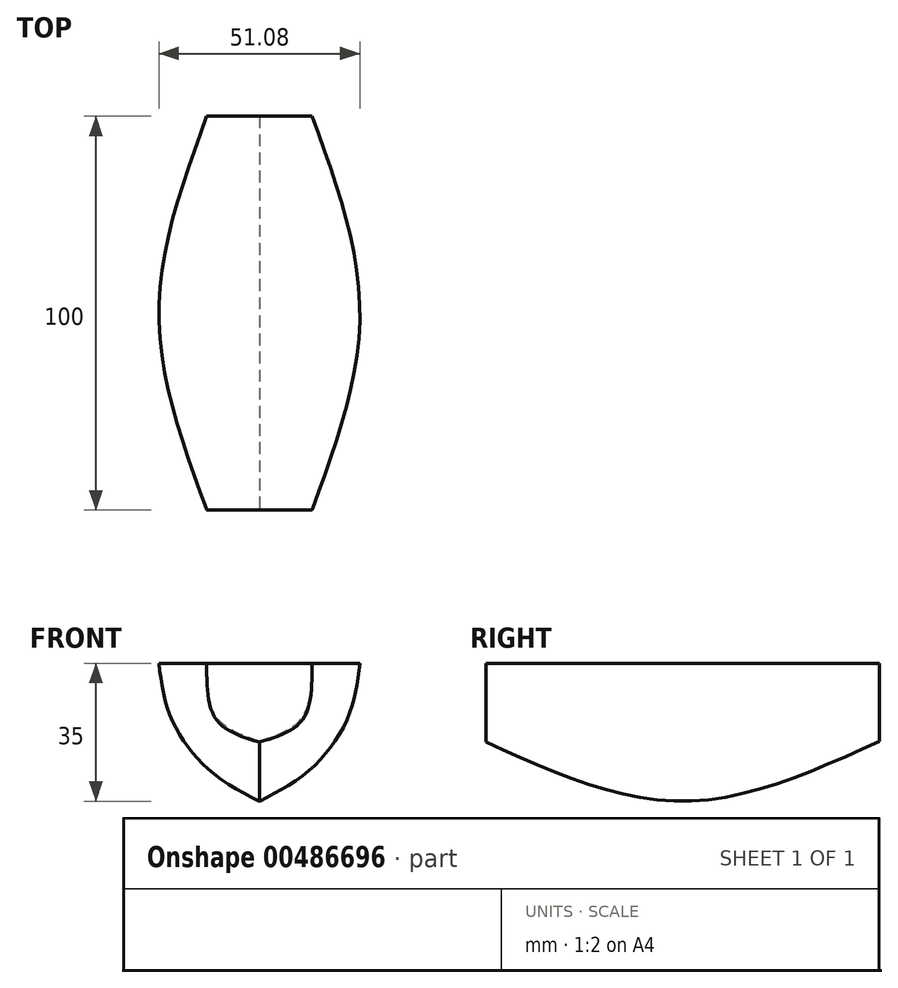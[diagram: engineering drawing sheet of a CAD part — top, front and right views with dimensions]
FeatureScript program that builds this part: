
annotation { "Feature Type Name" : "Feature", "Feature Type Description" : "" }
export const myFeature = defineFeature(function(context is Context, id is Id, definition is map)
    precondition{}
    {
        {
            var Q0;
            Q0=qCreatedBy(makeId("Front.planeOp"),FACE);
            cPlane(context, id + "F0", {"entities" : qUnion([Q0]), "cplaneType" : CPlaneType.OFFSET, "offset" : 50 * mm, "width" : 150 * mm, "height" : 150 * mm});
        }
        {
            var Q0;
            Q0=qCreatedBy(makeId("Front.planeOp"),FACE);
            cPlane(context, id + "F1", {"entities" : qUnion([Q0]), "cplaneType" : CPlaneType.OFFSET, "offset" : 50 * mm, "oppositeDirection" : true, "width" : 150 * mm, "height" : 150 * mm});
        }
        {
            var Q0;
            Q0=qCreatedBy(id+"F0.planeOp",FACE);
            var sketch = newSketch(context, id + "F2", { "sketchPlane" : qUnion([Q0])});
            skLineSegment(sketch, "E0", {"start": v(0, 0) * mm, "end": v(0, -20) * mm});
            skFitSpline(sketch, "E1", {"points": [v(0, -20) * mm, v(-10.95, -14.3) * mm, v(-13.38, 0) * mm], "startDerivative": vector(-27.16, 8.16) * mm, "endDerivative": vector(0.04, 31.53) * mm});
            skLineSegment(sketch, "E2", {"start": v(-13.38, 0) * mm, "end": v(0, 0) * mm});
            skSolve(sketch);
        }
        {
            var Q0;
            Q0=qCreatedBy(makeId("Front.planeOp"),FACE);
            var sketch = newSketch(context, id + "F3", { "sketchPlane" : qUnion([Q0])});
            skLineSegment(sketch, "E3", {"start": v(0, 0) * mm, "end": v(0, -35) * mm});
            skFitSpline(sketch, "E4", {"points": [v(0, -35) * mm, v(-12.77, -27.06) * mm, v(-22.5, -13.68) * mm, v(-25.54, 0) * mm], "startDerivative": vector(-40, 20.43) * mm, "endDerivative": vector(-5.44, 42.86) * mm});
            skLineSegment(sketch, "E5", {"start": v(-25.54, 0) * mm, "end": v(0, 0) * mm});
            skSolve(sketch);
        }
        {
            var Q0;
            Q0=qCreatedBy(id+"F1.planeOp",FACE);
            var sketch = newSketch(context, id + "F4", { "sketchPlane" : qUnion([Q0])});
            skLineSegment(sketch, "E6", {"start": v(0, 0) * mm, "end": v(0, -19.76) * mm});
            skFitSpline(sketch, "E7", {"points": [v(0, -19.76) * mm, v(-10.95, -13.68) * mm, v(-13.38, 0) * mm], "startDerivative": vector(-26.8, 9.03) * mm, "endDerivative": vector(-0.2, 30.3) * mm});
            skLineSegment(sketch, "E8", {"start": v(-13.38, 0) * mm, "end": v(0, 0) * mm});
            skSolve(sketch);
        }
        {
            var Q0;
            Q0 = qSketchRegion(id + "F4", true);
            var Q1;
            Q1 = qSketchRegion(id + "F3", true);
            var Q2;
            Q2 = qSketchRegion(id + "F2", true);
            loft(context, id + "F5", {"sheetProfilesArray" : [{ "sheetProfileEntities" : qUnion([Q0]) }, { "sheetProfileEntities" : qUnion([Q1]) }, { "sheetProfileEntities" : qUnion([Q2]) }]});
        }
        {
            var Q0;
            Q0=makeQuery(id+"F5.opLoft","SWEPT_BODY",BODY,{"disambiguationData":[OSD([makeQuery(id+"F2.imprint","IMPRINT",FACE,{"disambiguationData":[TD([[makeQuery(id+"F2.imprint","IMPRINT",EDGE,{"derivedFrom":sQuery(id+"F2.wireOp",EDGE,"E0")}),-1.0]])]}),sQuery(id+"F3.wireOp",EDGE,"E5"),makeQuery(id+"F4.imprint","IMPRINT",FACE,{"disambiguationData":[TD([[makeQuery(id+"F4.imprint","IMPRINT",EDGE,{"derivedFrom":sQuery(id+"F4.wireOp",EDGE,"E6")}),-1.0]])]})])]});
            var Q1;
            Q1=qCreatedBy(makeId("Right.planeOp"),FACE);
            mirror(context, id + "F6", {"operationType" : NewBodyOperationType.ADD, "entities" : qUnion([Q0]), "mirrorPlane" : qUnion([Q1])});
        }
    });
